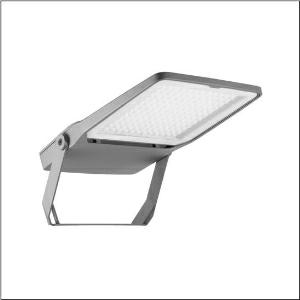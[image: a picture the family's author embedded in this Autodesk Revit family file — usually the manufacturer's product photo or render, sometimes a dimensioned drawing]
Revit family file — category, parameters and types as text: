
# Revit family: floodlight_fl_20_midi___pl61_5xa7681d2c1ac_c278
name_source: partatom
category: Lighting Fixtures
units: mm (PartAtom-declared; Revit-internal decimal feet)

## family parameters
Cut with Voids When Loaded = No
Host = Face
Light Source = No
Part Type = Normal
Room Calculation Point = No
Round Connector Dimension = Use Diameter
Shared = No

## types (1)
- Floodlight FL 20 midi  PL61 (1 x LED 4000K / CRI = 70 (unbekannt), 18200 lm, 4000K)
    Apparent Load = 142 VA
    CIE Flux Codes = 33 65 98 100 100
    Color Rendering = 70
    Color Temperature = 4000K
    Default Elevation = 1800 mm
    Description = Floodlight FL 20 midi, floodlight, primary light control with lens, of plastic, primary optical cover: protective disc, of toughened safety glass, transparent, light distribution: PL61, light emission: direct distribution, primary light characteristic: asymmetric, installation type: surface-mounted, LED, High Power LED, rated luminous flux: 18.200lm, luminous efficacy: 128lm/W, light colour: 740, colour temperature: 4000K, control gear: ECG Basic, control: power reduction, overheat protection, electronic power reduction, with terminal, 5-pole, max. 2.5mm², mains connection: 220..240V, AC, 50/60Hz, rated input power: 142W, LED unit, of diecast aluminium, powder-coated, Siteco® metallic grey (DB 702S), corrosivity category C5 mid according to DIN EN ISO 12944, incl. 1x M20 cable gland for cable Ø 6.5..12mm, length: 654mm, width: 450mm, height: 76mm, housing frame, of diecast aluminium, powder-coated, Siteco® metallic grey (DB 702S), mounting bracket, of steel, powder-coated, Siteco® metallic grey (DB 702S), ON/OFF, protection rating (complete): IP66, insulation class (complete): insulation class I (protective earthing), certification: CE, ENEC, VDE, protection symbol: D, permissible operating ambient temperature: -40..+40°C, permissible operating ambient temperature for outdoor applications: -40..+50°C, standard: DIN EN 12944, packaging unit: 1 piece

Light Distribution: PL61
    Height = 76 mm
    Lamp = 1 x LED 4000K / CRI >= 70 (unbekannt)
    Lamp Light Flux = 18200 lm
    Lamp count = 1
    Length = 672 mm
    Luminous efficacy = 128 lm/W
    Manufacturer = Siteco
    ModVariant = No
    Model = 5XA7681D2C1AC
    Mounting Place = Wall
    Mounting Type = Surface mounted
    Number of Poles = 1
    OnlyDefault = Yes
    Power Factor = 1
    Product Name = Floodlight FL 20 midi | PL61
    Product group = floodlight | wall mounted
    ProductGroupID = 2001
    Protection Class = Protection class I
    Protection Degree = IP 66
    RLX_Detail_Level = 1
    RLX_Emergency_Light_Flux = 0 lm
    RLX_Emergency_Type = 0
    RLX_Emergency_Type_DB = No
    RlxData = <blob elided: 94257 chars, md5=ff5a2a84>
    Socket = socket
    Standby Power = 0 W
    System Light Flux = 18200 lm
    System Power = 142 W
    Type Comments = Product without accessories
    Type Image = l_1005943.jpg
    URL = http://relux.com
    VarID = ---
    Voltage = 0 V
    Weight = 0.00 kg
    Width = 450 mm

## geometry (parser evidence)
native form markers: Blend x4, Sweep x13
no freeform markers — native parametric forms only
